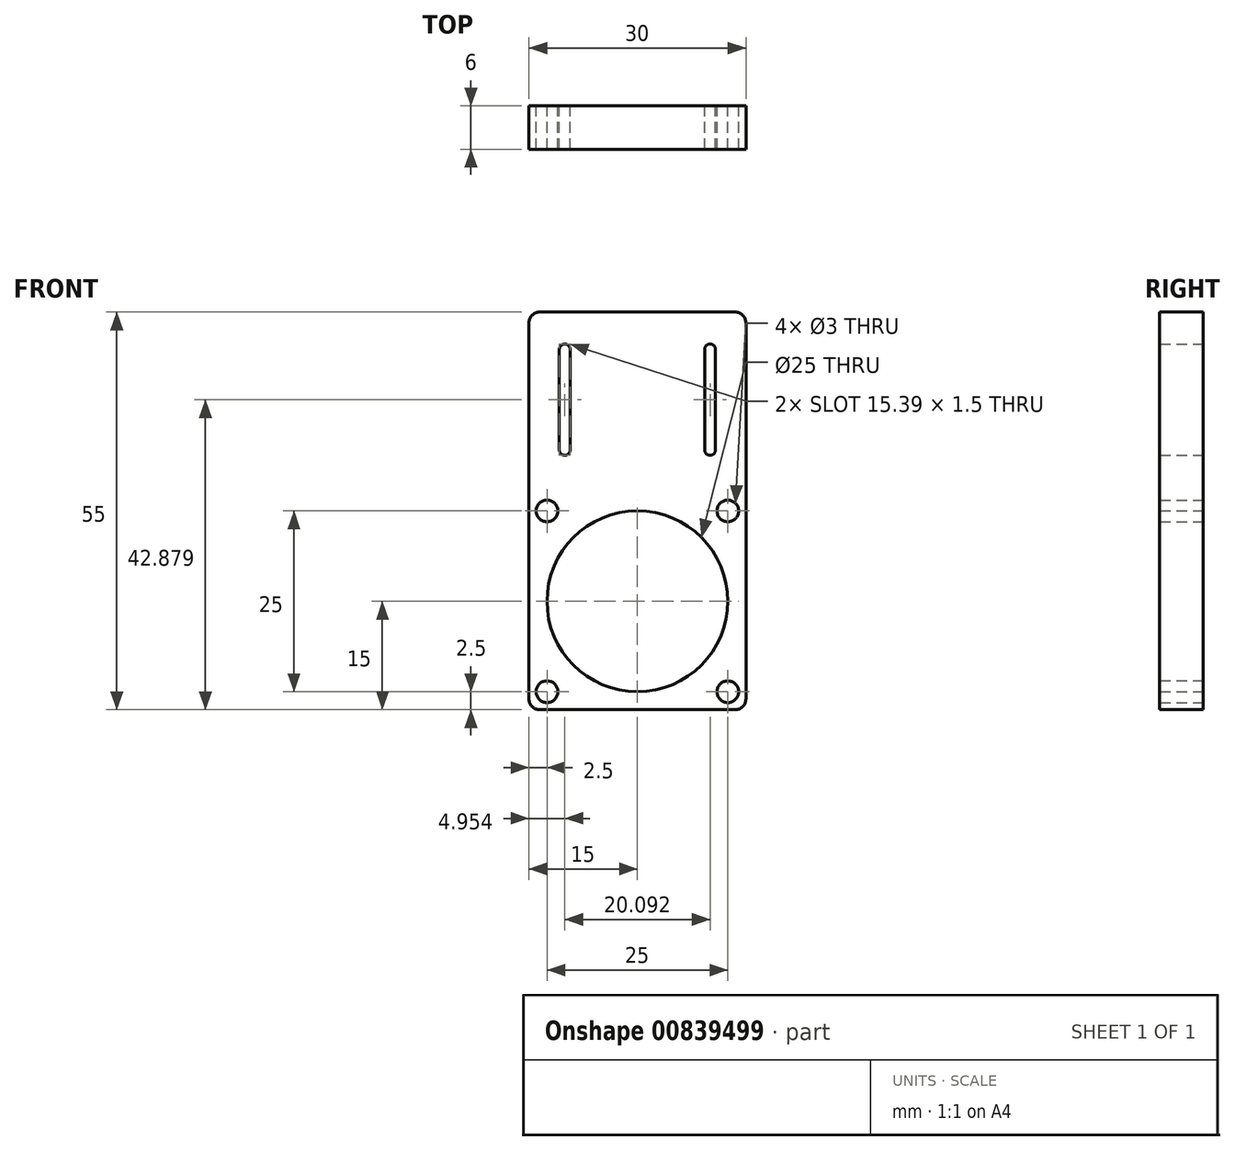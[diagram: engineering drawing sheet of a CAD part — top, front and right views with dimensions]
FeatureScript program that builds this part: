
annotation { "Feature Type Name" : "Feature", "Feature Type Description" : "" }
export const myFeature = defineFeature(function(context is Context, id is Id, definition is map)
    precondition{}
    {
        {
            var Q0;
            Q0=qCreatedBy(makeId("Front.planeOp"),FACE);
            var sketch = newSketch(context, id + "F0", { "sketchPlane" : qUnion([Q0])});
            skLineSegment(sketch, "E0.bottom", {"start": v(13.5, -27.5) * mm, "end": v(-13.5, -27.5) * mm});
            skLineSegment(sketch, "E0.top", {"start": v(13.5, 27.5) * mm, "end": v(-13.5, 27.5) * mm});
            skLineSegment(sketch, "E0.left", {"start": v(15, -26) * mm, "end": v(15, 26) * mm});
            skLineSegment(sketch, "E0.right", {"start": v(-15, -26) * mm, "end": v(-15, 26) * mm});
            skPoint(sketch, "E0.middle", {"position": v(0, 0) * mm});
            skLineSegment(sketch, "E1", {"start": v(0, -27.5) * mm, "end": v(0, -25) * mm, "construction": true});
            skLineSegment(sketch, "E2", {"start": v(0, -25) * mm, "end": v(0, -12.5) * mm, "construction": true});
            skCircle(sketch, "E3", {"center": v(0, -12.5) * mm, "radius": 12.5 * mm});
            skLineSegment(sketch, "E4", {"start": v(0, -12.5) * mm, "end": v(12.5, -12.5) * mm, "construction": true});
            skLineSegment(sketch, "E5", {"start": v(12.5, -12.5) * mm, "end": v(12.5, -25) * mm, "construction": true});
            skCircle(sketch, "E6", {"center": v(12.5, -25) * mm, "radius": 1.5 * mm});
            skCircle(sketch, "E7.1.0", {"center": v(12.5, 0) * mm, "radius": 1.5 * mm});
            skCircle(sketch, "E7.2.0", {"center": v(-12.5, 0) * mm, "radius": 1.5 * mm});
            skCircle(sketch, "E7.3.0", {"center": v(-12.5, -25) * mm, "radius": 1.5 * mm});
            skLineSegment(sketch, "E8", {"start": v(0, 8.43) * mm, "end": v(-10.05, 8.43) * mm, "construction": true});
            skLineSegment(sketch, "E9", {"start": v(-10.05, 8.43) * mm, "end": v(-10.05, 22.33) * mm, "construction": true});
            skArc(sketch, "E10.0.startCap", {"start": v(-9.3, 8.43) * mm, "mid": v(-10.05, 7.68) * mm, "end": v(-10.8, 8.43) * mm});
            skArc(sketch, "E10.0.endCap", {"start": v(-10.8, 22.33) * mm, "mid": v(-10.05, 23.08) * mm, "end": v(-9.3, 22.33) * mm});
            skLineSegment(sketch, "E10.0.left", {"start": v(-10.8, 8.43) * mm, "end": v(-10.8, 22.33) * mm});
            skLineSegment(sketch, "E10.0.right", {"start": v(-9.3, 8.43) * mm, "end": v(-9.3, 22.33) * mm});
            skLineSegment(sketch, "E11.MirrorCS", {"start": v(10.05, 8.43) * mm, "end": v(10.05, 22.33) * mm, "construction": true});
            skLineSegment(sketch, "E12.MirrorCS", {"start": v(0, 8.43) * mm, "end": v(10.05, 8.43) * mm, "construction": true});
            skLineSegment(sketch, "E13.MirrorCS", {"start": v(10.8, 8.43) * mm, "end": v(10.8, 22.33) * mm});
            skArc(sketch, "E14.MirrorCS", {"start": v(10.8, 22.33) * mm, "mid": v(10.05, 23.08) * mm, "end": v(9.3, 22.33) * mm});
            skArc(sketch, "E15.MirrorCS", {"start": v(9.3, 8.43) * mm, "mid": v(10.05, 7.68) * mm, "end": v(10.8, 8.43) * mm});
            skLineSegment(sketch, "E16.MirrorCS", {"start": v(9.3, 8.43) * mm, "end": v(9.3, 22.33) * mm});
            skPoint(sketch, "E17.visualSharp", {"position": v(-15, 27.5) * mm});
            skArc(sketch, "E17.filletArc", {"start": v(-13.5, 27.5) * mm, "mid": v(-14.56, 27.06) * mm, "end": v(-15, 26) * mm});
            skPoint(sketch, "E18.visualSharp", {"position": v(15, 27.5) * mm});
            skArc(sketch, "E18.filletArc", {"start": v(15, 26) * mm, "mid": v(14.56, 27.06) * mm, "end": v(13.5, 27.5) * mm});
            skPoint(sketch, "E19.visualSharp", {"position": v(15, -27.5) * mm});
            skArc(sketch, "E19.filletArc", {"start": v(13.5, -27.5) * mm, "mid": v(14.56, -27.06) * mm, "end": v(15, -26) * mm});
            skPoint(sketch, "E20.visualSharp", {"position": v(-15, -27.5) * mm});
            skArc(sketch, "E20.filletArc", {"start": v(-15, -26) * mm, "mid": v(-14.56, -27.06) * mm, "end": v(-13.5, -27.5) * mm});
            skSolve(sketch);
        }
        {
            var Q0;
            Q0=makeQuery(id+"F0.imprint","IMPRINT",FACE,{"disambiguationData":[TD([[makeQuery(id+"F0.imprint","IMPRINT",EDGE,{"derivedFrom":sQuery(id+"F0.wireOp",EDGE,"E0.bottom")}),-1.0]])]});
            extrude(context, id + "F1", {"entities" : qUnion([Q0]), "depth" : 6 * mm, "offsetDistance" : 25 * mm});
        }
    });
